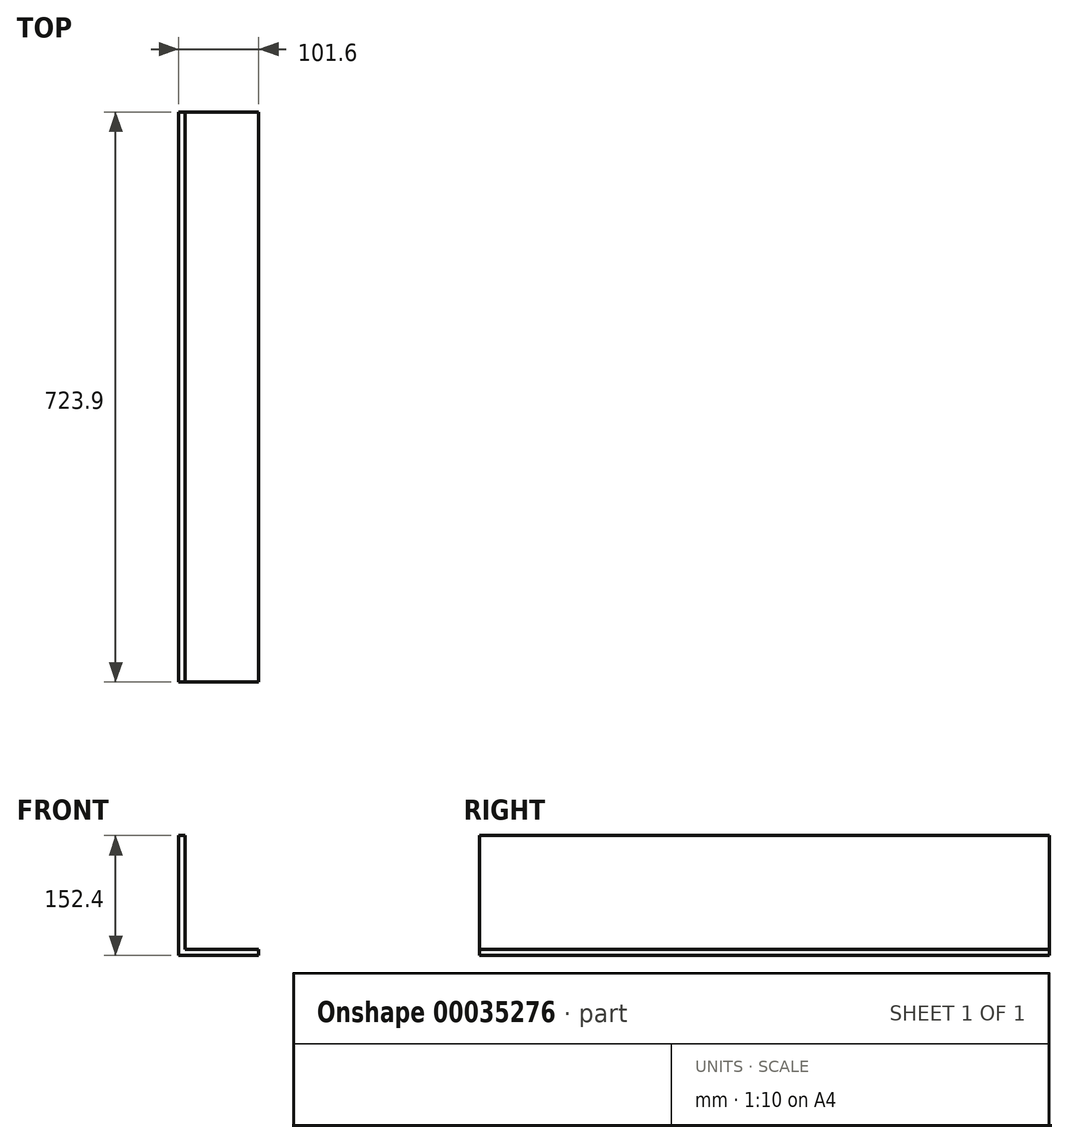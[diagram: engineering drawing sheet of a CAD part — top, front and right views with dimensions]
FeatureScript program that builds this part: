
annotation { "Feature Type Name" : "Feature", "Feature Type Description" : "" }
export const myFeature = defineFeature(function(context is Context, id is Id, definition is map)
    precondition{}
    {
        {
            var Q0;
            Q0=qCreatedBy(makeId("Front.planeOp"),FACE);
            var sketch = newSketch(context, id + "F0", { "sketchPlane" : qUnion([Q0])});
            skLineSegment(sketch, "E0", {"start": v(0, 0) * mm, "end": v(0, 152.4) * mm});
            skLineSegment(sketch, "E1", {"start": v(0, 0) * mm, "end": v(101.6, 0) * mm});
            skLineSegment(sketch, "E2.0", {"start": v(7.94, 7.94) * mm, "end": v(7.94, 152.4) * mm});
            skLineSegment(sketch, "E2.1", {"start": v(7.94, 7.94) * mm, "end": v(101.6, 7.94) * mm});
            skLineSegment(sketch, "E3", {"start": v(101.6, 0) * mm, "end": v(101.6, 7.94) * mm});
            skLineSegment(sketch, "E4", {"start": v(7.94, 152.4) * mm, "end": v(0, 152.4) * mm});
            skSolve(sketch);
        }
        {
            var Q0;
            Q0 = qSketchRegion(id + "F0", true);
            extrude(context, id + "F1", {"entities" : qUnion([Q0]), "depth" : 723.9 * mm});
        }
    });
